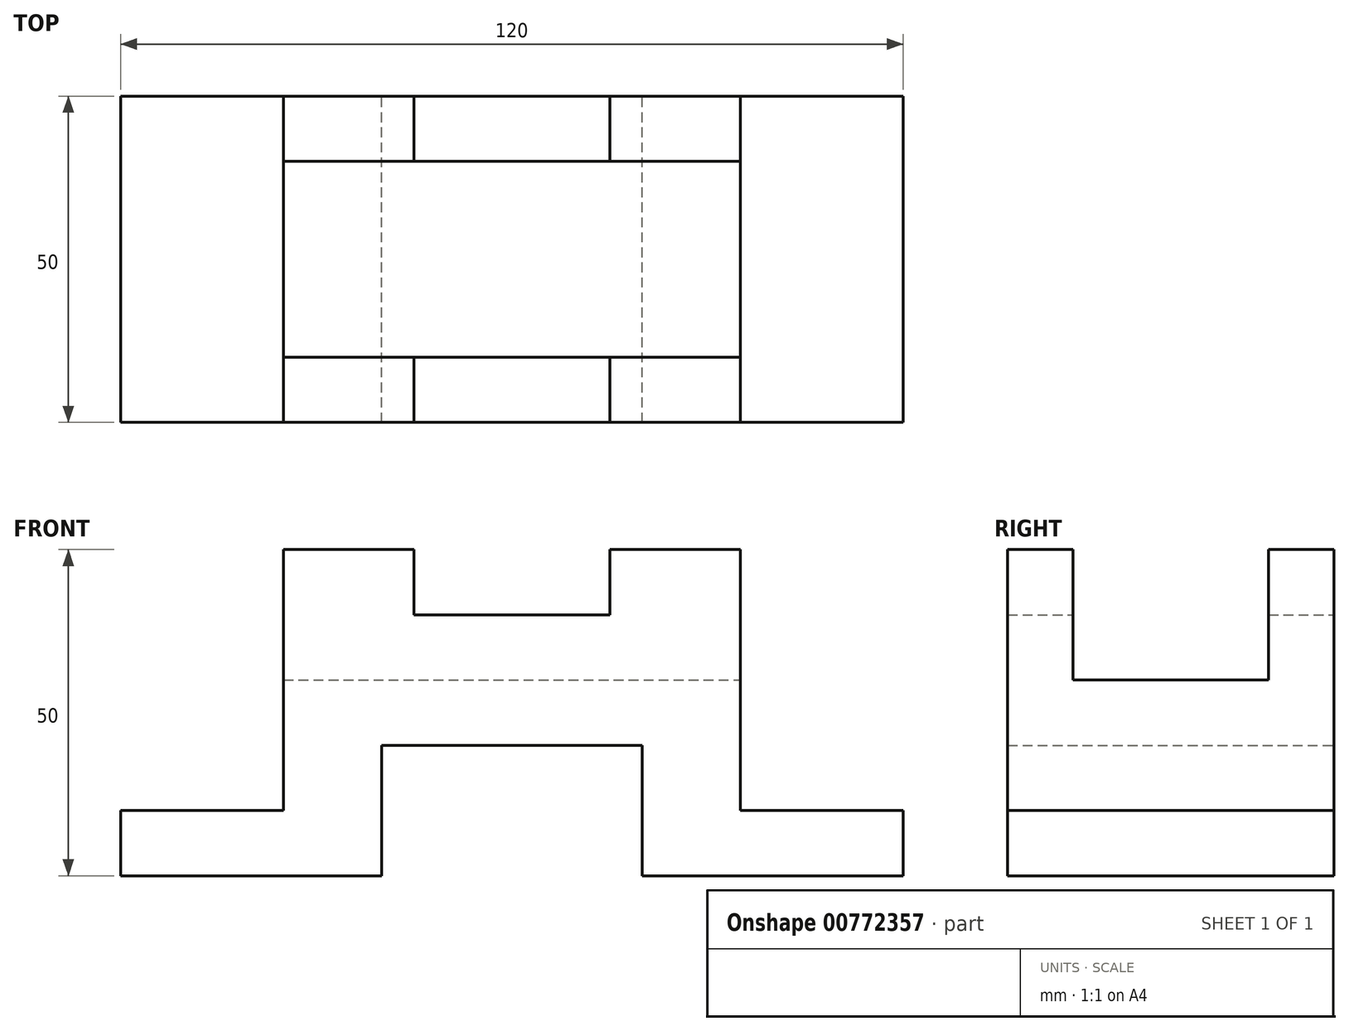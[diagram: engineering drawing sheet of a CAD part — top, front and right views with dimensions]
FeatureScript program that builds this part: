
annotation { "Feature Type Name" : "Feature", "Feature Type Description" : "" }
export const myFeature = defineFeature(function(context is Context, id is Id, definition is map)
    precondition{}
    {
        {
            var Q0;
            Q0=qCreatedBy(makeId("Front.planeOp"),FACE);
            var sketch = newSketch(context, id + "F0", { "sketchPlane" : qUnion([Q0])});
            skLineSegment(sketch, "E0", {"start": v(-60, 0) * mm, "end": v(-60, 10) * mm});
            skLineSegment(sketch, "E1", {"start": v(-60, 10) * mm, "end": v(-35, 10) * mm});
            skLineSegment(sketch, "E2", {"start": v(-35, 10) * mm, "end": v(-35, 50) * mm});
            skLineSegment(sketch, "E3", {"start": v(-35, 50) * mm, "end": v(-15, 50) * mm});
            skLineSegment(sketch, "E4", {"start": v(-15, 50) * mm, "end": v(-15, 40) * mm});
            skLineSegment(sketch, "E5", {"start": v(-15, 40) * mm, "end": v(0, 40) * mm});
            skLineSegment(sketch, "E6", {"start": v(-60, 0) * mm, "end": v(-20, 0) * mm});
            skLineSegment(sketch, "E7", {"start": v(-20, 0) * mm, "end": v(-20, 20) * mm});
            skLineSegment(sketch, "E8", {"start": v(-20, 20) * mm, "end": v(0, 20) * mm});
            skLineSegment(sketch, "E9", {"start": v(0, 40) * mm, "end": v(0, 20) * mm, "construction": true});
            skLineSegment(sketch, "E10.MirrorCS", {"start": v(15, 40) * mm, "end": v(0, 40) * mm});
            skLineSegment(sketch, "E11.MirrorCS", {"start": v(15, 50) * mm, "end": v(15, 40) * mm});
            skLineSegment(sketch, "E12.MirrorCS", {"start": v(60, 0) * mm, "end": v(60, 10) * mm});
            skLineSegment(sketch, "E13.MirrorCS", {"start": v(35, 10) * mm, "end": v(35, 50) * mm});
            skLineSegment(sketch, "E14.MirrorCS", {"start": v(60, 10) * mm, "end": v(35, 10) * mm});
            skLineSegment(sketch, "E15.MirrorCS", {"start": v(60, 0) * mm, "end": v(20, 0) * mm});
            skLineSegment(sketch, "E16.MirrorCS", {"start": v(35, 50) * mm, "end": v(15, 50) * mm});
            skLineSegment(sketch, "E17.MirrorCS", {"start": v(20, 20) * mm, "end": v(0, 20) * mm});
            skLineSegment(sketch, "E18.MirrorCS", {"start": v(20, 0) * mm, "end": v(20, 20) * mm});
            skLineSegment(sketch, "E19", {"start": v(-35, 30) * mm, "end": v(35, 30) * mm});
            skSolve(sketch);
        }
        {
            var Q0;
            Q0=makeQuery(id+"F0.imprint","IMPRINT",FACE,{"disambiguationData":[TD([[makeQuery(id+"F0.imprint","IMPRINT",EDGE,{"derivedFrom":sQuery(id+"F0.wireOp",EDGE,"E0")}),-1.0]])]});
            var Q1;
            {var subQ1=sQuery(id+"F0.wireOp",EDGE,"E3");Q1=makeQuery(id+"F0.imprint","IMPRINT",FACE,{"disambiguationData":[TD([[makeQuery(id+"F0.imprint","IMPRINT",EDGE,{"derivedFrom":subQ1}),-1.0]])]});}
            extrude(context, id + "F1", {"entities" : qUnion([Q0, Q1]), "endBound" : BoundingType.SYMMETRIC, "depth" : 50 * mm, "offsetDistance" : 25 * mm});
        }
        {
            var Q0;
            {var subQ1=sQuery(id+"F0.wireOp",EDGE,"E3");Q0=makeQuery(id+"F0.imprint","IMPRINT",FACE,{"disambiguationData":[TD([[makeQuery(id+"F0.imprint","IMPRINT",EDGE,{"derivedFrom":subQ1}),-1.0]])]});}
            extrude(context, id + "F2", {"entities" : qUnion([Q0]), "operationType" : NewBodyOperationType.REMOVE, "endBound" : BoundingType.SYMMETRIC, "oppositeDirection" : true, "depth" : 30 * mm, "offsetDistance" : 25 * mm});
        }
    });
